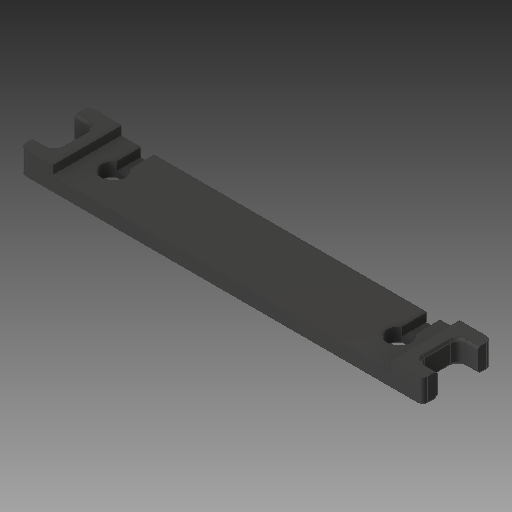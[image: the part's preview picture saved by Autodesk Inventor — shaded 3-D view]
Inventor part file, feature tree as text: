
AUTODESK INVENTOR PART (.ipt)
format: ipt  version: 2019 (Build 230136000, 136)  size: 222,208 bytes
history: native  units: mm
features: other x5, extrude x4, fillet x1, chamfer x1
ambient origin geometry x8: Origin, YZ Plane, XZ Plane, XY Plane, X Axis, Y Axis, Z Axis, Center Point
bodies: Solid1 (feature_tree), Body (feature_tree)
feature tree (11):
  extrude  "Body Cutout"  Depth=30.0mm
  extrude  "Rail Cutouts"  Depth=15.0mm
  extrude  "Spigot Cutouts"  Depth=176.0mm
  extrude  "Spigot Supports"  Depth=88.0mm
  fillet  "Body Fillet"  Radius=10.0mm
  chamfer  "Rail Cutouts Chamfer"  Distance=14.0mm
  other  "Body Outline"
  other  "Body Cutout Outline"
  other  "Rail Cutouts Outline"
  other  "Spigot Cutouts Outline"
  other  "Spigot Supports Outline"
